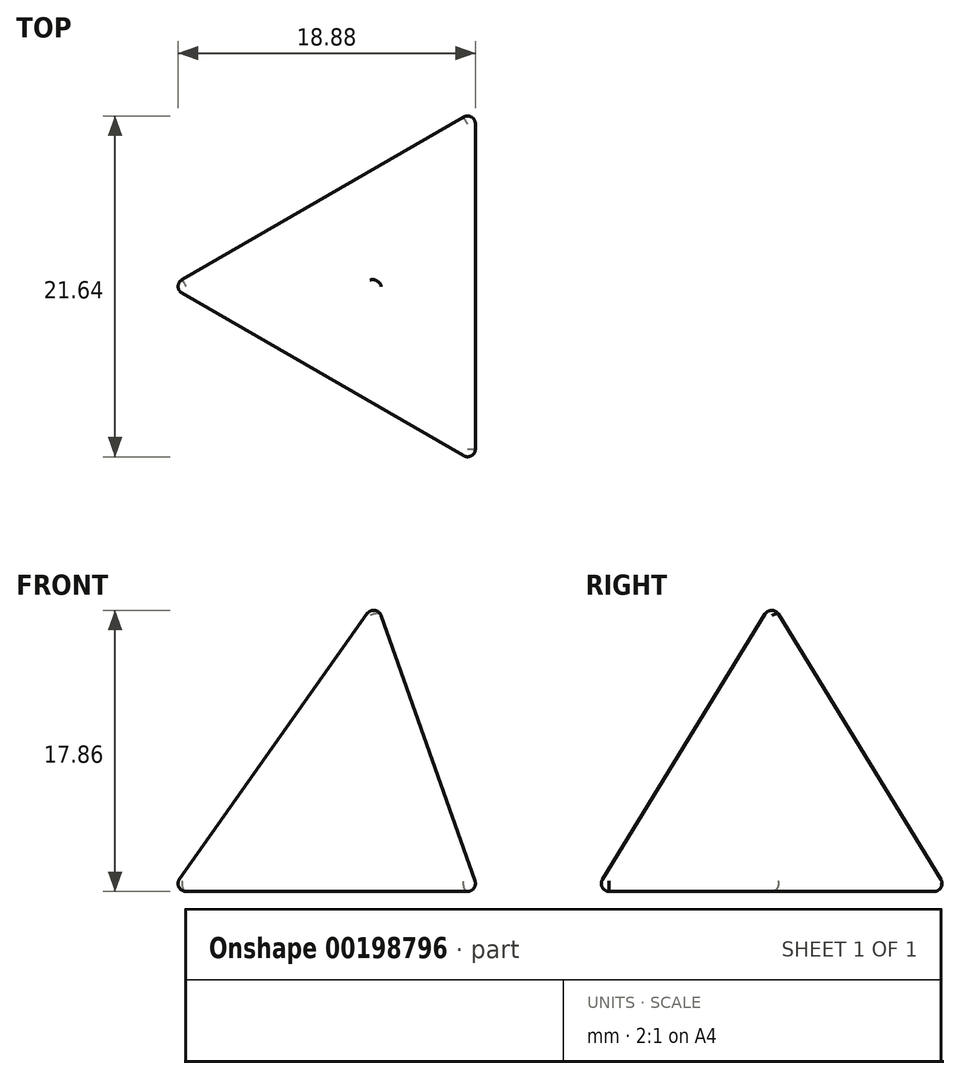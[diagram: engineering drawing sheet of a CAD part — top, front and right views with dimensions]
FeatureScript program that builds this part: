
annotation { "Feature Type Name" : "Feature", "Feature Type Description" : "" }
export const myFeature = defineFeature(function(context is Context, id is Id, definition is map)
    precondition{}
    {
        {
            assignVariable(context, id + "F0", {"name" : "kulma", "anyValue" : 90 * degree - acos(1 / 3)});
        }
        {
            var Q0;
            Q0=qCreatedBy(makeId("Top.planeOp"),FACE);
            var sketch = newSketch(context, id + "F1", { "sketchPlane" : qUnion([Q0])});
            skCircle(sketch, "E0.cCircle", {"center": v(0, 0) * mm, "radius": 6.67 * mm, "construction": true});
            skLineSegment(sketch, "E0.0", {"start": v(6.67, 11.55) * mm, "end": v(6.67, -11.55) * mm});
            skLineSegment(sketch, "E0.1", {"start": v(6.67, -11.55) * mm, "end": v(-13.33, 0) * mm});
            skLineSegment(sketch, "E0.2", {"start": v(-13.33, 0) * mm, "end": v(6.67, 11.55) * mm});
            skPoint(sketch, "E0.0.midPoint", {"position": v(6.67, 0) * mm});
            skSolve(sketch);
        }
        {
            var Q0;
            Q0=makeQuery(id+"F1.imprint","IMPRINT",FACE,{"disambiguationData":[TD([[makeQuery(id+"F1.imprint","IMPRINT",EDGE,{"derivedFrom":sQuery(id+"F1.wireOp",EDGE,"E0.0")}),-1.0]])]});
            extrude(context, id + "F2", {"entities" : qUnion([Q0]), "depth" : 25 * mm, "hasDraft" : true, "draftAngle" : getVariable(context, 'kulma'), "draftPullDirection" : true});
        }
        {
            var Q0;
            Q0=makeQuery(id+"F2.opExtrude","SWEPT_FACE",FACE,{"disambiguationData":[OSD([sQuery(id+"F1.wireOp",EDGE,"E0.0")])]});
            var Q1;
            Q1=makeQuery(id+"F2.opExtrude","SWEPT_EDGE",EDGE,{"disambiguationData":[OSD([sQuery(id+"F1.wireOp",EDGE,"E0.0"),sQuery(id+"F1.wireOp",EDGE,"E0.2")])]});
            var Q2;
            Q2=makeQuery(id+"F2.opExtrude","SWEPT_FACE",FACE,{"disambiguationData":[OSD([sQuery(id+"F1.wireOp",EDGE,"E0.1")])]});
            var Q3;
            Q3=makeQuery(id+"F2.opExtrude","SWEPT_EDGE",EDGE,{"disambiguationData":[OSD([sQuery(id+"F1.wireOp",EDGE,"E0.1"),sQuery(id+"F1.wireOp",EDGE,"E0.2")])]});
            var Q4;
            Q4=makeQuery(id+"F2.opExtrude","CAP_FACE",FACE,{"disambiguationData":[OSD([sQuery(id+"F1.wireOp",EDGE,"E0.0"),sQuery(id+"F1.wireOp",EDGE,"E0.1"),sQuery(id+"F1.wireOp",EDGE,"E0.2")])],"isStart":true});
            var Q5;
            Q5=makeQuery(id+"F2.opExtrude","CAP_EDGE",EDGE,{"disambiguationData":[OSD([sQuery(id+"F1.wireOp",EDGE,"E0.0")])],"isStart":true});
            var Q6;
            Q6=makeQuery(id+"F2.opExtrude","CAP_EDGE",EDGE,{"disambiguationData":[OSD([sQuery(id+"F1.wireOp",EDGE,"E0.1")])],"isStart":true});
            var Q7;
            Q7=makeQuery(id+"F2.opExtrude","SWEPT_EDGE",EDGE,{"disambiguationData":[OSD([sQuery(id+"F1.wireOp",EDGE,"E0.0"),sQuery(id+"F1.wireOp",EDGE,"E0.1")])]});
            var Q8;
            Q8=makeQuery(id+"F2.opExtrude","SWEPT_FACE",FACE,{"disambiguationData":[OSD([sQuery(id+"F1.wireOp",EDGE,"E0.2")])]});
            var Q9;
            Q9=makeQuery(id+"F2.opExtrude","CAP_EDGE",EDGE,{"disambiguationData":[OSD([sQuery(id+"F1.wireOp",EDGE,"E0.2")])],"isStart":true});
            fillet(context, id + "F3", {"entities" : qUnion([Q0, Q1, Q2, Q3, Q4, Q5, Q6, Q7, Q8, Q9]), "radius" : 0.5 * mm, "tangentPropagation" : true, "allowEdgeOverflow" : false});
        }
    });
